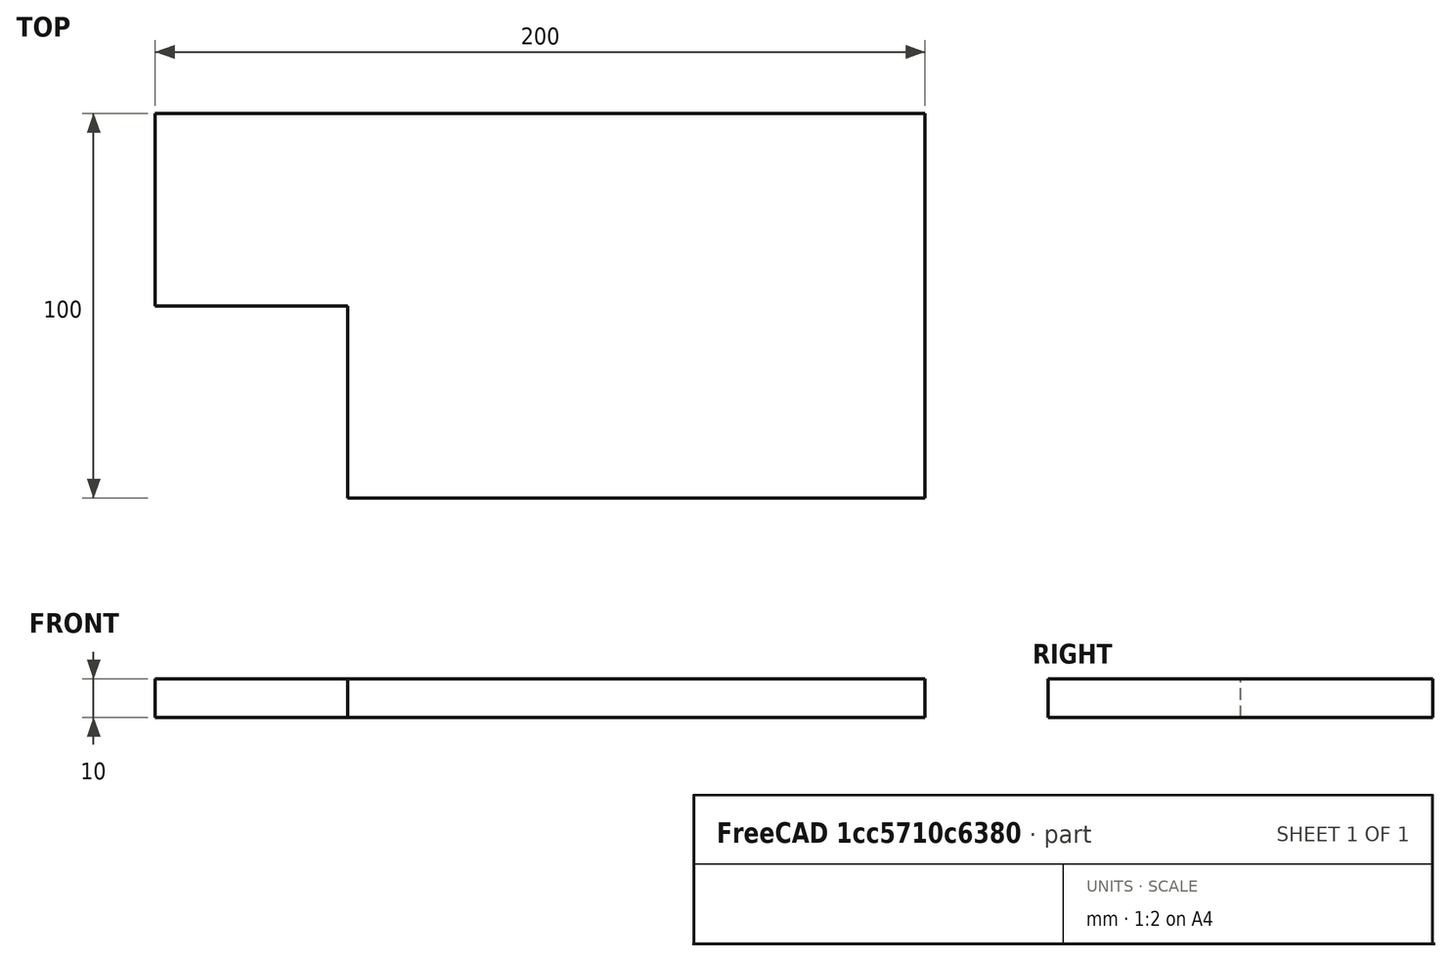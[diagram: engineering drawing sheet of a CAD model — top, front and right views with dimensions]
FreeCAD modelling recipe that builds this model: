
FCSTD DOCUMENT  (FreeCAD 0.21R33694 (Git))
Label: Plate_with_square_hole_Example
License: All rights reserved
LicenseURL: http://en.wikipedia.org/wiki/All_rights_reserved
objects: Fem::ConstraintDisplacement×3, Part::Box×2, App::MaterialObjectPython×1, Fem::FemSolverObjectPython×1, Part::Cut×1, Fem::ConstraintPressure×1, Fem::FemMeshObjectPython×1, Fem::FemAnalysis×1
note: 3 computed .brp shape members not serialized (recipe doc carries the construction recipe); baked Part::Feature solids carry a one-line shape summary decoded from their .brp

FEATURE [Part::Box] Box  label="Cube"
  AttacherType = Attacher::AttachEngine3D
  Height = 10
  Length = 200
  Width = 100
FEATURE [App::MaterialObjectPython] SolidMaterial  # material (typed FeaturePython)
  Category = 0
  Material = Density=7900.0 kg/m^3,Description=Standard steel material for CalculiX sample calculations,Father=Metal,Name=CalculiX-Steel,PoissonRatio=0.3,+4 more (map truncated)
FEATURE [Fem::FemSolverObjectPython] SolverCcxTools  # FEM object (typed FeaturePython)
  AnalysisType = 0
  BeamShellResultOutput3D = false
  BucklingFactors = 1
  EigenmodeHighLimit = 1000000
  EigenmodeLowLimit = 0
  EigenmodesCount = 10
  GeometricalNonlinearity = 1
  IterationsControlParameterCutb = 0.25,0.5,0.75,0.85,,,1.5,
  IterationsControlParameterIter = 4,8,9,200,10,400,,200,,
  IterationsControlParameterTimeUse = false
  IterationsThermoMechMaximum = 200
  IterationsUserDefinedIncrementations = false
  IterationsUserDefinedTimeStepLength = false
  MaterialNonlinearity = 1
  MatrixSolverType = 0
  SplitInputWriter = false
  ThermoMechSteadyState = true
  TimeEnd = 1
  TimeInitialStep = 1
FEATURE [Part::Box] Box001  label="Cube001"
  AttacherType = Attacher::AttachEngine3D
  Height = 10
  Length = 100
  Placement = pos=(-50,-50,0) rot=(0,0,1;0rad)
  Width = 100
FEATURE [Part::Cut] Cut
  Base = -> Box
  Tool = -> Box001
FEATURE [Fem::ConstraintDisplacement] FemConstraintDisplacement
  NormalDirection = (-1,0,0)
  Normals = (12) [(-1,0,0),(-1,0,0),(-1,0,0),(-1,0,0),(-1,0,0),(-1,0,0),(-1,0,0),(-1,0,0),(-1,0,0),(-1,0,0),(-1,0,0),(-1,0,0)]
  Points = (12) [(0,100,0),(0,100,5),(0,100,10),(0,83.3333,0),(0,83.3333,5),(0,83.3333,10),(0,66.6667,0),(0,66.6667,5),(0,66.6667,10),(0,50,0),(0,50,5),(0,50,10)]
  References = -> [Cut]
  hasXFormula = false
  hasYFormula = false
  hasZFormula = false
  rotxFix = false
  rotxFree = true
  rotyFix = false
  rotyFree = true
  rotzFix = false
  rotzFree = true
  useFlowSurfaceForce = false
  xDisplacement = 0
  xFix = true
  xFree = false
  xRotation = 0
  yDisplacement = 0
  yFix = false
  yFree = true
  yRotation = 0
  zDisplacement = 0
  zFix = false
  zFree = true
  zRotation = 0
FEATURE [Fem::ConstraintDisplacement] FemConstraintDisplacement001
  NormalDirection = (0,-1,0)
  Normals = (12) [(0,-1,0),(0,-1,0),(0,-1,0),(0,-1,0),(0,-1,0),(0,-1,0),(0,-1,0),(0,-1,0),(0,-1,0),(0,-1,0),(0,-1,0),(0,-1,0)]
  Points = (12) [(50,0,0),(50,0,5),(50,0,10),(100,0,0),(100,0,5),(100,0,10),(150,0,0),(150,0,5),(150,0,10),(200,0,0),(200,0,5),(200,0,10)]
  References = -> [Cut]
  hasXFormula = false
  hasYFormula = false
  hasZFormula = false
  rotxFix = false
  rotxFree = true
  rotyFix = false
  rotyFree = true
  rotzFix = false
  rotzFree = true
  useFlowSurfaceForce = false
  xDisplacement = 0
  xFix = false
  xFree = true
  xRotation = 0
  yDisplacement = 0
  yFix = true
  yFree = false
  yRotation = 0
  zDisplacement = 0
  zFix = false
  zFree = true
  zRotation = 0
FEATURE [Fem::ConstraintPressure] FemConstraintPressure
  NormalDirection = (1,0,0)
  Normals = (12) [(1,0,0),(1,0,0),(1,0,0),(1,0,0),(1,0,0),(1,0,0),(1,0,0),(1,0,0),(1,0,0),(1,0,0),(1,0,0),(1,0,0)]
  Points = (12) [(200,100,0),(200,100,5),(200,100,10),(200,66.6667,0),(200,66.6667,5),(200,66.6667,10),(200,33.3333,0),(200,33.3333,5),(200,33.3333,10),(200,0,0),+2 more]
  Pressure = 50
  References = -> [Cut]
  Reversed = true
FEATURE [Fem::ConstraintDisplacement] FemConstraintDisplacement002
  NormalDirection = (0,0,-1)
  Normals = (14) [(0,0,-1),(0,0,-1),(0,0,-1),(0,0,-1),(0,0,-1),(0,0,-1),(0,0,-1),(0,0,-1),(0,0,-1),(0,0,-1),(0,0,-1),(0,0,-1),(0,0,-1),(0,0,-1)]
  Points = (14) [(66.6667,0,0),(133.333,0,0),(200,0,0),(66.6667,33.3333,0),(133.333,33.3333,0),(200,33.3333,0),(0,66.6667,0),(66.6667,66.6667,0),(133.333,66.6667,0),+5 more]
  References = -> [Cut]
  Scale = 13
  hasXFormula = false
  hasYFormula = false
  hasZFormula = false
  rotxFix = false
  rotxFree = true
  rotyFix = false
  rotyFree = true
  rotzFix = false
  rotzFree = true
  useFlowSurfaceForce = false
  xDisplacement = 0
  xFix = false
  xFree = true
  xRotation = 0
  yDisplacement = 0
  yFix = false
  yFree = true
  yRotation = 0
  zDisplacement = 0
  zFix = true
  zFree = false
  zRotation = 0
FEATURE [Fem::FemMeshObjectPython] FEMMeshGmsh  # FEM object (typed FeaturePython)
  Algorithm2D = 0
  Algorithm3D = 0
  CharacteristicLengthMax = 0
  CharacteristicLengthMin = 0
  CoherenceMesh = true
  ElementDimension = 0
  ElementOrder = 1
  GeometryTolerance = 1e-06
  GroupsOfNodes = false
  HighOrderOptimize = 0
  MeshSizeFromCurvature = 12
  OptimizeNetgen = false
  OptimizeStd = true
  Part = -> Cut
  RecombinationAlgorithm = 0
  Recombine3DAll = false
  RecombineAll = false
  SecondOrderLinear = false
FEATURE [Fem::FemAnalysis] Analysis
  Group = -> [SolverCcxTools,FemConstraintDisplacement,FemConstraintDisplacement001,FemConstraintPressure,SolidMaterial,FemConstraintDisplacement002,FEMMeshGmsh]
